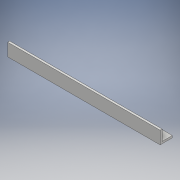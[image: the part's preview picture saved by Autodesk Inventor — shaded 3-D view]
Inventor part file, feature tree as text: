
AUTODESK INVENTOR PART (.ipt)
format: ipt  version: 2018 (Build 220112000, 112)  size: 105,984 bytes
history: native  units: mm
features: extrude x2, sketch x2, projected_geometry x1
ambient origin geometry x8: Origin, YZ Plane, XZ Plane, XY Plane, X Axis, Y Axis, Z Axis, Center Point
bodies: Solid1 (feature_tree)
feature tree (5):
  extrude  "Extrusion1"  Depth=16.0mm
  extrude  "Extrusion2"  Depth=16.0mm
  sketch  "Sketch1"  dims[d0=1200.0mm d1=16.0mm]
  sketch  "Sketch2"  dims[d2=100.0mm d3=0.0mm d4=16.0mm d5=80.0mm d6=0.0mm]
  projected_geometry  "Projected Loop1"
